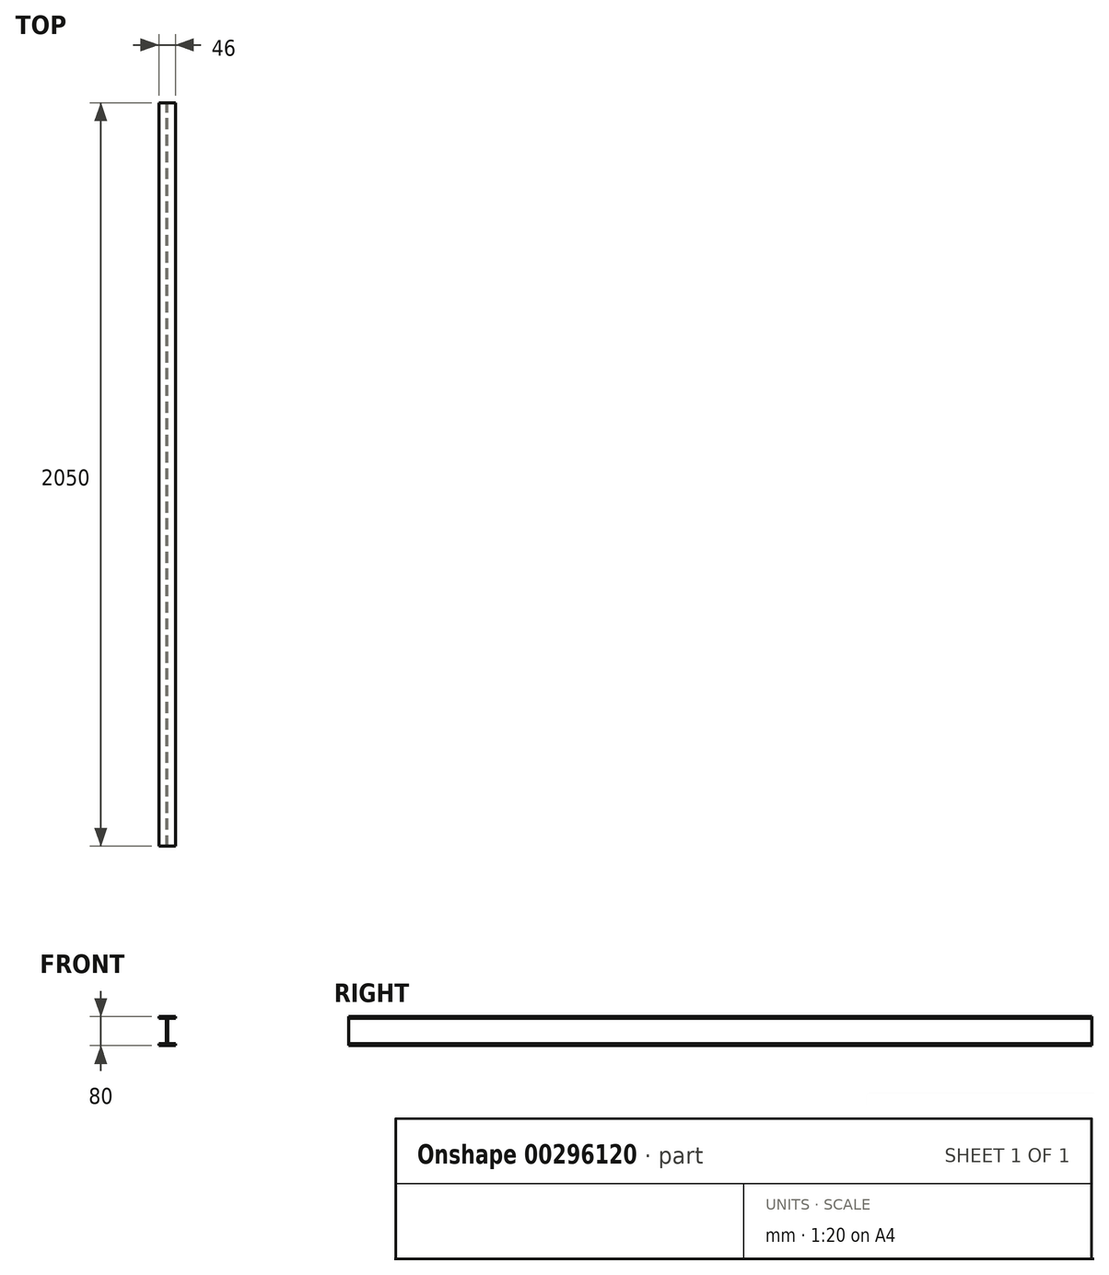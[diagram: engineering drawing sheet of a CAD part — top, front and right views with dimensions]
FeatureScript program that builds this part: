
annotation { "Feature Type Name" : "Feature", "Feature Type Description" : "" }
export const myFeature = defineFeature(function(context is Context, id is Id, definition is map)
    precondition{}
    {
        {
            var Q0;
            Q0=qCreatedBy(makeId("Front.planeOp"),FACE);
            var sketch = newSketch(context, id + "F0", { "sketchPlane" : qUnion([Q0])});
            skLineSegment(sketch, "E0.right", {"start": v(-23, 40) * mm, "end": v(-23, 34.8) * mm});
            skPoint(sketch, "E0.middle", {"position": v(0, 0) * mm});
            skLineSegment(sketch, "E1", {"start": v(-23, 34.8) * mm, "end": v(-6.9, 34.8) * mm});
            skLineSegment(sketch, "E2", {"start": v(-1.9, 29.8) * mm, "end": v(-1.9, 0) * mm});
            skPoint(sketch, "E0.top.end.orphan", {"position": v(-23, -40) * mm});
            skPoint(sketch, "E0.top.start.orphan", {"position": v(23, -40) * mm});
            skLineSegment(sketch, "E3.MirrorCS", {"start": v(-23, -40) * mm, "end": v(-23, -34.8) * mm});
            skLineSegment(sketch, "E4.MirrorCS", {"start": v(-23, -34.8) * mm, "end": v(-6.9, -34.8) * mm});
            skLineSegment(sketch, "E5.MirrorCS", {"start": v(-1.9, -29.8) * mm, "end": v(-1.9, 0) * mm});
            skPoint(sketch, "E0.bottom.start.orphan", {"position": v(23, 40) * mm});
            skLineSegment(sketch, "E6", {"start": v(-23, 40) * mm, "end": v(0, 40) * mm});
            skLineSegment(sketch, "E7", {"start": v(-23, -40) * mm, "end": v(0, -40) * mm});
            skLineSegment(sketch, "E8.MirrorCS", {"start": v(23, 40) * mm, "end": v(23, 34.8) * mm});
            skLineSegment(sketch, "E9.MirrorCS", {"start": v(23, -40) * mm, "end": v(23, -34.8) * mm});
            skLineSegment(sketch, "E10.MirrorCS", {"start": v(23, -40) * mm, "end": v(0, -40) * mm});
            skLineSegment(sketch, "E11.MirrorCS", {"start": v(1.9, -29.8) * mm, "end": v(1.9, 0) * mm});
            skLineSegment(sketch, "E12.MirrorCS", {"start": v(23, 40) * mm, "end": v(0, 40) * mm});
            skLineSegment(sketch, "E13.MirrorCS", {"start": v(23, 34.8) * mm, "end": v(6.9, 34.8) * mm});
            skLineSegment(sketch, "E14.MirrorCS", {"start": v(23, -34.8) * mm, "end": v(6.9, -34.8) * mm});
            skLineSegment(sketch, "E15.MirrorCS", {"start": v(1.9, 29.8) * mm, "end": v(1.9, 0) * mm});
            skPoint(sketch, "E16.visualSharp", {"position": v(-1.9, 34.8) * mm});
            skArc(sketch, "E16.filletArc", {"start": v(-1.9, 29.8) * mm, "mid": v(-3.36, 33.34) * mm, "end": v(-6.9, 34.8) * mm});
            skPoint(sketch, "E17.visualSharp", {"position": v(1.9, 34.8) * mm});
            skArc(sketch, "E17.filletArc", {"start": v(6.9, 34.8) * mm, "mid": v(3.36, 33.34) * mm, "end": v(1.9, 29.8) * mm});
            skPoint(sketch, "E18.visualSharp", {"position": v(1.9, -34.8) * mm});
            skArc(sketch, "E18.filletArc", {"start": v(1.9, -29.8) * mm, "mid": v(3.36, -33.34) * mm, "end": v(6.9, -34.8) * mm});
            skPoint(sketch, "E19.visualSharp", {"position": v(-1.9, -34.8) * mm});
            skArc(sketch, "E19.filletArc", {"start": v(-6.9, -34.8) * mm, "mid": v(-3.36, -33.34) * mm, "end": v(-1.9, -29.8) * mm});
            skSolve(sketch);
        }
        {
            var Q0;
            Q0 = qSketchRegion(id + "F0", true);
            extrude(context, id + "F1", {"entities" : qUnion([Q0]), "depth" : 2050 * mm});
        }
    });
